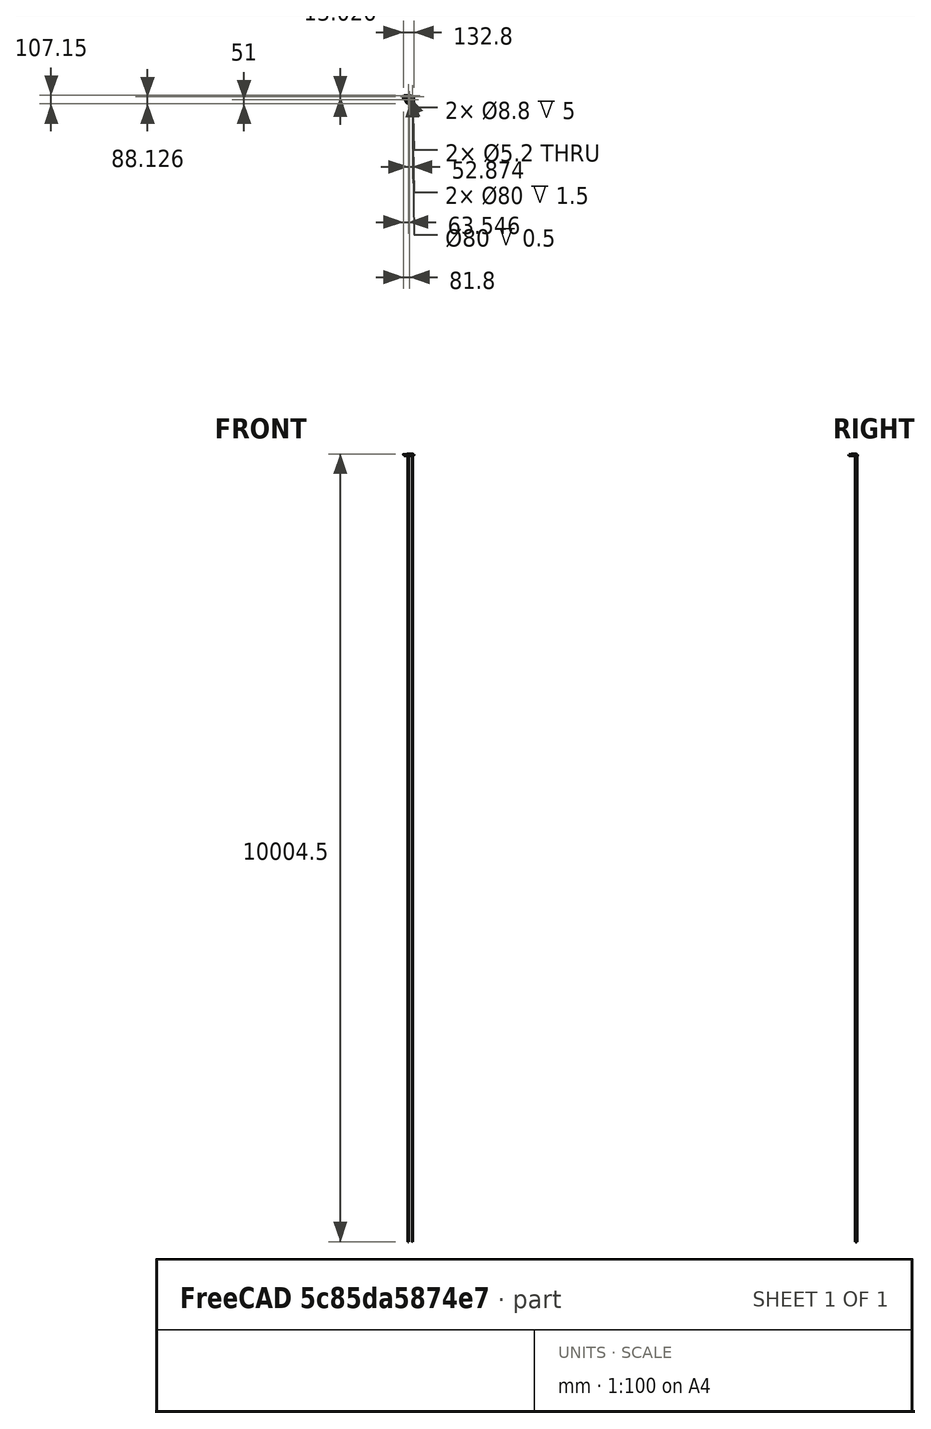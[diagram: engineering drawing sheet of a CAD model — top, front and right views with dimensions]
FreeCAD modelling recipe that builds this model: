
FCSTD DOCUMENT  (FreeCAD 0.16R)
Label: SimpleChainguard_RC1
License: All rights reserved
LicenseURL: http://en.wikipedia.org/wiki/All_rights_reserved
objects: Sketcher::SketchObject×7, Part::Cylinder×4, PartDesign::Fillet×4, PartDesign::Pad×3, PartDesign::Pocket×3, Part::Cut×2, PartDesign::Revolution×1, Part::MultiFuse×1, PartDesign::Chamfer×1, Mesh::Feature×1
note: 33 computed .brp shape members not serialized (recipe doc carries the construction recipe); baked Part::Feature solids carry a one-line shape summary decoded from their .brp

FEATURE [Sketcher::SketchObject] Sketch
  sketch-geometry (7):
    g0: Circle CenterX=0 CenterY=0 CenterZ=0 NormalX=0 NormalY=0 NormalZ=1 Radius=40
    g1: ArcOfCircle CenterX=0 CenterY=0 CenterZ=0 NormalX=0 NormalY=0 NormalZ=1 Radius=51 StartAngle=3.54457 EndAngle=7.85398
    g2: LineSegment StartX=-75 StartY=51 StartZ=0 EndX=0 EndY=51 EndZ=0
    g3: ArcOfCircle CenterX=-54.8043 CenterY=33.0798 CenterZ=0 NormalX=0 NormalY=0 NormalZ=1 Radius=27 StartAngle=2.41582 EndAngle=4.05122
    g4: ArcOfCircle CenterX=-120.507 CenterY=-51.3726 CenterZ=0 NormalX=0 NormalY=0 NormalZ=1 Radius=80 StartAngle=0.402976 EndAngle=0.909627
    g5: LineSegment [constr] StartX=0 StartY=0 StartZ=0 EndX=114.907 EndY=96.4181 EndZ=0
    g6: LineSegment [constr] StartX=-46.3525 StartY=142.658 StartZ=0 EndX=0 EndY=0 EndZ=0
  constraints (22):
    c: Radius(g0) = 40
    c: Coincident(g0,g-1)
    c: Coincident(g1,g-1)
    c: PointOnObject(g1,g-2)
    c: Coincident(g2,g1)
    c: Horizontal(g2)
    c: Distance(g2) = 75
    c: Coincident(g3,g2)
    c: Coincident(g4,g3)
    c: Coincident(g4,g1)
    c: Tangent(g4,g3)
    c: Tangent(g1,g4)
    c: Radius(g1) = 51
    c: Radius(g4) = 80
    c: Radius(g3) = 27
    c: Coincident(g5,g-1)
    c: Angle(g6) = -1.25664
    c: Coincident(g6,g-1)
    c: Angle(g5) = 0.698132
    c: Distance(g5) = 150
    c: Distance(g6) = 150
    c: DistanceY(g1) = -20
FEATURE [PartDesign::Pad] Pad
  Length = 1.5
  Length2 = 100
  Sketch = -> Sketch
  Type = 0
FEATURE [Sketcher::SketchObject] Sketch004
  Placement = pos=(0,0,0) rot=(0.57735,0.57735,0.57735;2.0944rad)
  sketch-geometry (8):
    g0: LineSegment StartX=48.364 StartY=-12.364 StartZ=0 EndX=45.8891 EndY=-9.88909 EndZ=0
    g1: ArcOfCircle CenterX=42 CenterY=-6 CenterZ=0 NormalX=0 NormalY=0 NormalZ=1 Radius=5.5 StartAngle=5.49779 EndAngle=6.28319
    g2: ArcOfCircle CenterX=42 CenterY=-6 CenterZ=0 NormalX=0 NormalY=0 NormalZ=1 Radius=9 StartAngle=5.49779 EndAngle=6.28319
    g3: LineSegment [constr] StartX=35.4204 StartY=-25.3075 StartZ=0 EndX=48.364 EndY=-12.364 EndZ=0
    g4: LineSegment [constr] StartX=19.9837 StartY=-35.7944 StartZ=0 EndX=45.8891 EndY=-9.88909 EndZ=0
    g5: LineSegment StartX=47.5 StartY=-6 StartZ=0 EndX=47.5 EndY=0 EndZ=0
    g6: LineSegment StartX=51 StartY=-6 StartZ=0 EndX=51 EndY=0 EndZ=0
    g7: LineSegment StartX=47.5 StartY=0 StartZ=0 EndX=51 EndY=0 EndZ=0
  constraints (25):
    c: Coincident(g2,g1)
    c: Parallel(g3,g4)
    c: Angle(g4) = 0.785398
    c: Coincident(g0,g2)
    c: Coincident(g0,g1)
    c: Perpendicular(g2,g0)
    c: DistanceX(g1) = 42
    c: Distance(g3) = 18.3049
    c: Distance(g4) = 36.6357
    c: Coincident(g0,g3)
    c: Coincident(g4,g0)
    c: Tangent(g4,g1)
    c: DistanceX(g2) = 51
    c: Coincident(g5,g1)
    c: PointOnObject(g5,g-1)
    c: Coincident(g6,g2)
    c: PointOnObject(g6,g-1)
    c: Vertical(g6)
    c: Distance(g5) = 6
    c: Tangent(g1,g5)
    c: Vertical(g5)
    c: Tangent(g2,g6)
    c: Coincident(g7,g5)
    c: Coincident(g7,g6)
    c: Distance(g7) = 3.5
FEATURE [Part::Cylinder] Cylinder002
  Angle = 360
  Height = 8
  Placement = pos=(-17,27,-2) rot=(0,0,1;0rad)
  Radius = 20
FEATURE [Part::Cylinder] Cylinder003
  Angle = 360
  Height = 8
  Placement = pos=(12,12,-2) rot=(0,0,1;0rad)
  Radius = 30
FEATURE [PartDesign::Revolution] Revolution
  Angle = 180
  Axis = (0,0,1)
  Base = (0,0,0)
  Placement = pos=(0,0,0) rot=(0.57735,0.57735,0.57735;2.0944rad)
  ReferenceAxis = -> Sketch004 [V_Axis]
  Reversed = true
  Sketch = -> Sketch004
FEATURE [Sketcher::SketchObject] Sketch009
  Placement = pos=(0,0,0) rot=(0.57735,0.57735,0.57735;2.0944rad)
  sketch-geometry (8):
    g0: LineSegment StartX=48.364 StartY=-12.364 StartZ=0 EndX=45.8891 EndY=-9.88909 EndZ=0
    g1: ArcOfCircle CenterX=42 CenterY=-6 CenterZ=0 NormalX=0 NormalY=0 NormalZ=1 Radius=5.5 StartAngle=5.49779 EndAngle=6.28319
    g2: ArcOfCircle CenterX=42 CenterY=-6 CenterZ=0 NormalX=0 NormalY=0 NormalZ=1 Radius=9 StartAngle=5.49779 EndAngle=6.28319
    g3: LineSegment [constr] StartX=35.4204 StartY=-25.3075 StartZ=0 EndX=48.364 EndY=-12.364 EndZ=0
    g4: LineSegment [constr] StartX=19.9837 StartY=-35.7944 StartZ=0 EndX=45.8891 EndY=-9.88909 EndZ=0
    g5: LineSegment StartX=47.5 StartY=-6 StartZ=0 EndX=47.5 EndY=0 EndZ=0
    g6: LineSegment StartX=51 StartY=-6 StartZ=0 EndX=51 EndY=0 EndZ=0
    g7: LineSegment StartX=47.5 StartY=0 StartZ=0 EndX=51 EndY=0 EndZ=0
  constraints (25):
    c: Coincident(g2,g1)
    c: Parallel(g3,g4)
    c: Angle(g4) = 0.785398
    c: Coincident(g0,g2)
    c: Coincident(g0,g1)
    c: Perpendicular(g2,g0)
    c: DistanceX(g1) = 42
    c: Distance(g3) = 18.3049
    c: Distance(g4) = 36.6357
    c: Coincident(g0,g3)
    c: Coincident(g4,g0)
    c: Tangent(g4,g1)
    c: DistanceX(g2) = 51
    c: Coincident(g5,g1)
    c: PointOnObject(g5,g-1)
    c: Coincident(g6,g2)
    c: PointOnObject(g6,g-1)
    c: Vertical(g6)
    c: Distance(g5) = 6
    c: Tangent(g1,g5)
    c: Vertical(g5)
    c: Tangent(g2,g6)
    c: Coincident(g7,g5)
    c: Coincident(g7,g6)
    c: Distance(g7) = 3.5
FEATURE [PartDesign::Pad] Pad001
  Length = 75
  Length2 = 100
  Placement = pos=(0,0,0) rot=(0.57735,0.57735,0.57735;2.0944rad)
  Reversed = true
  Sketch = -> Sketch009
  Type = 0
FEATURE [Part::MultiFuse] Fusion
  Shapes = -> [Pad001,Revolution,Pad]
FEATURE [Sketcher::SketchObject] Sketch005
  Placement = pos=(0,0,1.5) rot=(0,0,1;0rad)
  Support = -> Fusion [Face5]
  sketch-geometry (4):
    g0: LineSegment [constr] StartX=-50.5793 StartY=138.966 StartZ=0 EndX=0 EndY=0 EndZ=0
    g1: LineSegment [constr] StartX=114.381 StartY=122.659 StartZ=0 EndX=0 EndY=0 EndZ=0
    g2: Circle CenterX=-18.2538 CenterY=50.1518 CenterZ=0 NormalX=0 NormalY=0 NormalZ=1 Radius=6
    g3: Circle CenterX=34.6201 CenterY=37.1256 CenterZ=0 NormalX=0 NormalY=0 NormalZ=1 Radius=6
  constraints (10):
    c: Coincident(g0,g-1)
    c: Coincident(g1,g-1)
    c: Angle(g1) = -2.32129
    c: Angle(g0) = -1.22173
    c: Radius(g2) = 6
    c: Radius(g3) = 6
    c: Distance(g-1,g2) = 53.3704
    c: Distance(g-1,g3) = 50.7628
    c: PointOnObject(g2,g0)
    c: PointOnObject(g3,g1)
FEATURE [PartDesign::Pad] Pad002
  Length = 21
  Length2 = 100
  Reversed = true
  Sketch = -> Sketch005
  Type = 0
FEATURE [Sketcher::SketchObject] Sketch012
  ExternalGeometry = -> [Pad002]
  Placement = pos=(0,0,1.5) rot=(0,0,1;0rad)
  Support = -> Pad002 [Face5]
  sketch-geometry (2):
    g0: Circle CenterX=-18.2538 CenterY=50.1518 CenterZ=0 NormalX=0 NormalY=0 NormalZ=1 Radius=2.6
    g1: Circle CenterX=34.6201 CenterY=37.1256 CenterZ=0 NormalX=0 NormalY=0 NormalZ=1 Radius=2.6
  constraints (4):
    c: Radius(g1) = 2.6
    c: Equal(g1,g0)
    c: Coincident(g0,g-3)
    c: Coincident(g1,g-4)
FEATURE [PartDesign::Pocket] Pocket
  Length = 5
  Sketch = -> Sketch012
  Type = 1
FEATURE [Sketcher::SketchObject] Sketch013
  ExternalGeometry = -> [Pocket]
  Placement = pos=(0,0,1.5) rot=(0,0,1;0rad)
  Support = -> Pocket [Face5]
  sketch-geometry (2):
    g0: Circle CenterX=-18.2538 CenterY=50.1518 CenterZ=0 NormalX=0 NormalY=0 NormalZ=1 Radius=4.4
    g1: Circle CenterX=34.6201 CenterY=37.1256 CenterZ=0 NormalX=0 NormalY=0 NormalZ=1 Radius=4.4
  constraints (4):
    c: Radius(g0) = 4.4
    c: Equal(g0,g1)
    c: Coincident(g1,g-4)
    c: Coincident(g0,g-3)
FEATURE [PartDesign::Pocket] Pocket001
  Length = 5
  Sketch = -> Sketch013
  Type = 0
FEATURE [Sketcher::SketchObject] Sketch008
  Placement = pos=(0,0,-19.5) rot=(1,0,0;3.14159rad)
  Support = -> Pocket001 [Face39]
  sketch-geometry (4):
    g0: LineSegment StartX=-35.7258 StartY=-32.8433 StartZ=0 EndX=0 EndY=-32.8433 EndZ=0
    g1: LineSegment StartX=0 StartY=-32.8433 StartZ=0 EndX=0 EndY=-68.5691 EndZ=0
    g2: LineSegment StartX=0 StartY=-68.5691 StartZ=0 EndX=-35.7258 EndY=-68.5691 EndZ=0
    g3: LineSegment StartX=-35.7258 StartY=-68.5691 StartZ=0 EndX=-35.7258 EndY=-32.8433 EndZ=0
  constraints (12):
    c: Coincident(g0,g1)
    c: Coincident(g1,g2)
    c: Coincident(g2,g3)
    c: Coincident(g3,g0)
    c: Horizontal(g0)
    c: Horizontal(g2)
    c: Vertical(g1)
    c: Vertical(g3)
    c: PointOnObject(g1,g-2)
    c: Equal(g0,g1)
    c: Distance(g1) = 35.7258
    c: DistanceY(g0) = -32.8433
FEATURE [PartDesign::Pocket] Pocket002
  Length = 1.5
  Sketch = -> Sketch008
  Type = 0
FEATURE [Part::Cylinder] Cylinder
  Angle = 360
  Height = 8
  Placement = pos=(0,0,-9) rot=(0,0,1;0rad)
  Radius = 46
FEATURE [Part::Cut] Cut
  Base = -> Pocket002
  Tool = -> Cylinder
FEATURE [Part::Cylinder] Cylinder004
  Angle = 360
  Height = 8
  Placement = pos=(-17,-1.8,-9) rot=(0,0,1;0rad)
  Radius = 48
FEATURE [Part::Cut] Cut001
  Base = -> Cut
  Tool = -> Cylinder004
FEATURE [PartDesign::Chamfer] Chamfer
  Base = -> Cut001 [Edge27]
  Size = 1
FEATURE [PartDesign::Fillet] Fillet
  Base = -> Chamfer [Edge134]
  Radius = 1
FEATURE [PartDesign::Fillet] Fillet001
  Base = -> Fillet [Edge60]
  Radius = 1
FEATURE [PartDesign::Fillet] Fillet002
  Base = -> Fillet001 [Edge128]
  Radius = 1
FEATURE [PartDesign::Fillet] Fillet003
  Base = -> Fillet002 [Edge42,Edge68]
  Radius = 1.5
FEATURE [Mesh::Feature] Mesh  label="Fillet003 (Meshed)"
